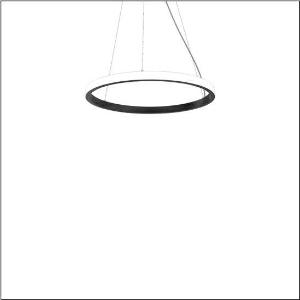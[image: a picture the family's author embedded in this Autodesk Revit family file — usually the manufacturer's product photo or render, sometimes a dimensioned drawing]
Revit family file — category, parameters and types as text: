
# Revit family: silica_r__21_ring-o_5pjbo2d1104a_b1b1
name_source: partatom
category: Lighting Fixtures
units: mm (PartAtom-declared; Revit-internal decimal feet)

## family parameters
Cut with Voids When Loaded = No
Host = Face
Light Source = No
Part Type = Normal
Room Calculation Point = No
Round Connector Dimension = Use Diameter
Shared = No

## types (1)
- Silica® 21 Ring-O (1 x LED, 4700 lm, 80 W, 3000K)
    Apparent Load = 80 VA
    CIE Flux Codes = 2 16 49 50 100
    Color Rendering = 80
    Color Temperature = 3000K
    Default Elevation = 1800 mm
    Description = Silica® 21 Ring-O, suspended luminaire, of PMMA, frosted, light emission: outer ring side luminous distribution, primary light characteristic: symmetric, installation type: suspended mounting, LED, rated luminous flux: 4.700lm, luminous efficacy: 59lm/W, light colour: 830, colour temperature: 3000K, with terminal, 5-pole, mains connection: 230V, AC/DC, 0/50..60Hz, rated input power: 80W, housing, of extruded aluminium section, jet black (RAL 9005), diameter: 810mm, ceiling canopy, jet black (RAL 9005), protection rating (lamp compartment): IP40, insulation class (complete): insulation class I (protective earthing), certification: CE, impact resistance: IK02, permissible operating ambient temperature: 0..+35°C, packaging unit: 1 piece
    Height = 48 mm
    Lamp = 1 x LED
    Lamp Light Flux = 4700 lm
    Lamp Power = 80 W
    Lamp count = 1
    Length = 810 mm
    Luminous efficacy = 59 lm/W
    Manufacturer = Siteco
    ModVariant = No
    Model = 5PJBO2D1104A
    Mounting Place = Ceiling
    Mounting Type = Pendant
    Number of Poles = 1
    OnlyDefault = Yes
    Power Factor = 1
    Product Name = Silica® 21 Ring-O
    Product group = suspended luminaire
    ProductGroupID = 904
    Protection Class = Protection class I
    Protection Degree = IP 40
    RLX_Detail_Level = 1
    RLX_Emergency_Light_Flux = 0 lm
    RLX_Emergency_Type = 0
    RLX_Emergency_Type_DB = No
    RlxData = <blob elided: 14065 chars, md5=36e12fa3>
    Socket = socket
    Standby Power = 0 W
    System Light Flux = 4700 lm
    System Power = 80 W
    Type Comments = Product without accessories
    Type Image = l_1258381.jpg
    URL = http://relux.com
    VarID = ---
    Voltage = 0 V
    Weight = 0.00 kg
    Width = 0 mm  [stored 0 ft]

note: [stored X ft] marks values corroborated as IEEE doubles in the binary element streams (Revit-internal decimal feet)

## geometry (parser evidence)
native form markers: Sweep x13
no freeform markers — native parametric forms only
